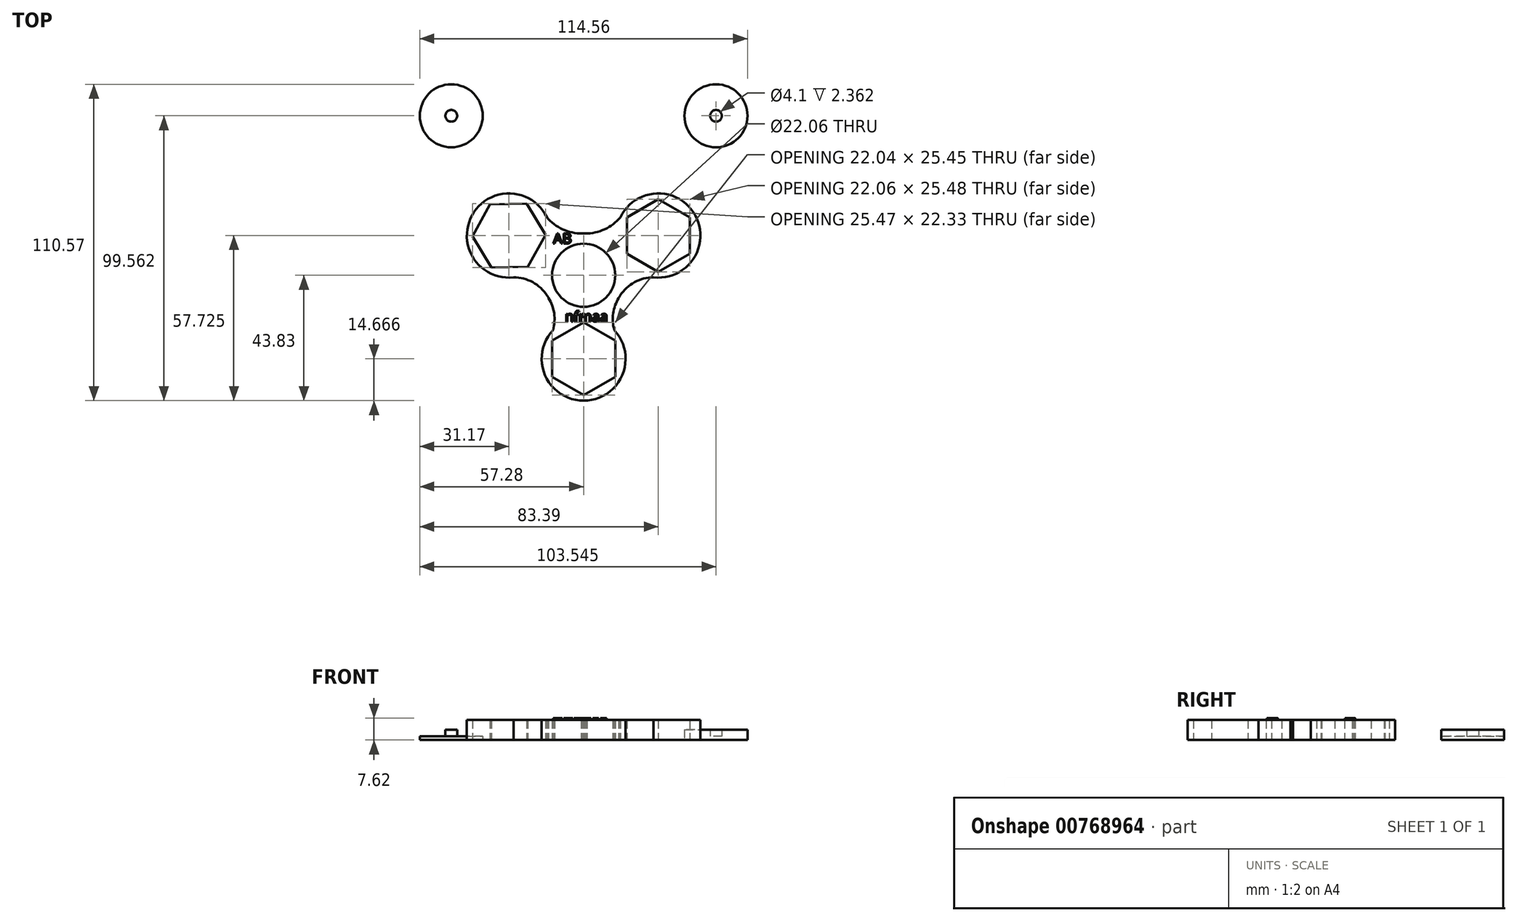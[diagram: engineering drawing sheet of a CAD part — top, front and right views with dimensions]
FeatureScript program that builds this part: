
annotation { "Feature Type Name" : "Feature", "Feature Type Description" : "" }
export const myFeature = defineFeature(function(context is Context, id is Id, definition is map)
    precondition{}
    {
        {
            var Q0;
            Q0=qCreatedBy(makeId("Top.planeOp"),FACE);
            var sketch = newSketch(context, id + "F0", { "sketchPlane" : qUnion([Q0])});
            skCircle(sketch, "E0", {"center": v(0, 0) * mm, "radius": 11.03 * mm});
            skCircle(sketch, "E1", {"center": v(0, 0) * mm, "radius": 14.6 * mm});
            skPoint(sketch, "E2", {"position": v(26.11, 13.9) * mm});
            skCircle(sketch, "E3", {"center": v(26.11, 13.9) * mm, "radius": 14.7 * mm});
            skPoint(sketch, "E4.MirrorP", {"position": v(-26.11, 13.9) * mm});
            skCircle(sketch, "E5.MirrorC", {"center": v(-26.11, 13.9) * mm, "radius": 14.7 * mm});
            skCircle(sketch, "E6", {"center": v(0, -29.16) * mm, "radius": 14.66 * mm});
            skLineSegment(sketch, "E7.0", {"start": v(-13.37, 14.17) * mm, "end": v(-19.5, 3) * mm});
            skLineSegment(sketch, "E7.1", {"start": v(-19.5, 3) * mm, "end": v(-32.24, 2.73) * mm});
            skLineSegment(sketch, "E7.2", {"start": v(-32.24, 2.73) * mm, "end": v(-38.85, 13.62) * mm});
            skLineSegment(sketch, "E7.3", {"start": v(-38.85, 13.62) * mm, "end": v(-32.71, 24.79) * mm});
            skLineSegment(sketch, "E7.4", {"start": v(-32.71, 24.79) * mm, "end": v(-19.98, 25.06) * mm});
            skLineSegment(sketch, "E7.5", {"start": v(-19.98, 25.06) * mm, "end": v(-13.37, 14.17) * mm});
            skLineSegment(sketch, "E8.0", {"start": v(37.14, 20.26) * mm, "end": v(37.14, 7.53) * mm});
            skLineSegment(sketch, "E8.1", {"start": v(37.14, 7.53) * mm, "end": v(26.11, 1.16) * mm});
            skLineSegment(sketch, "E8.2", {"start": v(26.11, 1.16) * mm, "end": v(15.08, 7.53) * mm});
            skLineSegment(sketch, "E8.3", {"start": v(15.08, 7.53) * mm, "end": v(15.08, 20.26) * mm});
            skLineSegment(sketch, "E8.4", {"start": v(15.08, 20.26) * mm, "end": v(26.11, 26.63) * mm});
            skLineSegment(sketch, "E8.5", {"start": v(26.11, 26.63) * mm, "end": v(37.14, 20.26) * mm});
            skLineSegment(sketch, "E9.0", {"start": v(-11.02, -35.53) * mm, "end": v(-11.02, -22.8) * mm});
            skLineSegment(sketch, "E9.1", {"start": v(-11.02, -22.8) * mm, "end": v(0, -16.44) * mm});
            skLineSegment(sketch, "E9.2", {"start": v(0, -16.44) * mm, "end": v(11.02, -22.8) * mm});
            skLineSegment(sketch, "E9.3", {"start": v(11.02, -22.8) * mm, "end": v(11.02, -35.53) * mm});
            skLineSegment(sketch, "E9.4", {"start": v(11.02, -35.53) * mm, "end": v(0, -41.89) * mm});
            skLineSegment(sketch, "E9.5", {"start": v(0, -41.89) * mm, "end": v(-11.02, -35.53) * mm});
            skArc(sketch, "E10", {"start": v(0, 14.6) * mm, "mid": v(7.07, 15.96) * mm, "end": v(12.85, 20.26) * mm});
            skArc(sketch, "E11.MirrorCS", {"start": v(0, 14.6) * mm, "mid": v(-7.07, 15.96) * mm, "end": v(-12.85, 20.26) * mm});
            skArc(sketch, "E12", {"start": v(26.11, -0.81) * mm, "mid": v(18.1, -2.27) * mm, "end": v(12.25, -7.95) * mm});
            skArc(sketch, "E13.MirrorCS", {"start": v(-26.11, -0.81) * mm, "mid": v(-18.1, -2.27) * mm, "end": v(-12.25, -7.95) * mm});
            skArc(sketch, "E14", {"start": v(12.25, -7.95) * mm, "mid": v(10.18, -15.38) * mm, "end": v(12.25, -22.8) * mm});
            skArc(sketch, "E15.MirrorCS", {"start": v(-12.25, -7.95) * mm, "mid": v(-10.18, -15.38) * mm, "end": v(-12.25, -22.8) * mm});
            skSolve(sketch);
        }
        {
            var Q0;
            Q0=qSketchRegion(id+"F0",true);
            extrude(context, id + "F1", {"entities" : qUnion([Q0]), "depth" : 7 * mm, "offsetDistance" : 25.4 * mm});
        }
        {
            var Q0;
            Q0=qCreatedBy(makeId("Top.planeOp"),FACE);
            var sketch = newSketch(context, id + "F2", { "sketchPlane" : qUnion([Q0])});
            skText(sketch, "E16", { "text": "nfmaa", "fontName": "OpenSans-Regular.ttf"});
            skText(sketch, "E17", { "text": "AB", "fontName": "OpenSans-Regular.ttf"});
            const initialGuessF2  = {"E16": [-0.00651, -0.01619, 1, 0, 0.0036], "E17": [-0.0106, 0.01111, 1, 0, 0.0036]};
            skSetInitialGuess(sketch, initialGuessF2);
            skSolve(sketch);
        }
        {
            var Q0;
            Q0=qSketchRegion(id+"F2",true);
            extrude(context, id + "F3", {"entities" : qUnion([Q0]), "operationType" : NewBodyOperationType.ADD, "depth" : 7.62 * mm, "offsetDistance" : 25.4 * mm});
        }
        {
            var Q0;
            Q0=qCreatedBy(makeId("Top.planeOp"),FACE);
            var sketch = newSketch(context, id + "F4", { "sketchPlane" : qUnion([Q0])});
            skCircle(sketch, "E18", {"center": v(-46.27, 55.73) * mm, "radius": 2.05 * mm});
            skCircle(sketch, "E19.MirrorC", {"center": v(46.27, 55.73) * mm, "radius": 2.05 * mm});
            skCircle(sketch, "E20", {"center": v(-46.27, 55.73) * mm, "radius": 11.01 * mm});
            skCircle(sketch, "E21.MirrorC", {"center": v(46.27, 55.73) * mm, "radius": 11.01 * mm});
            skSolve(sketch);
        }
        {
            var Q0;
            Q0=makeQuery(id+"F4.imprint","IMPRINT",FACE,{"disambiguationData":[TD([[makeQuery(id+"F4.imprint","IMPRINT",EDGE,{"derivedFrom":sQuery(id+"F4.wireOp",EDGE,"E18")}),1.0]])]});
            extrude(context, id + "F5", {"entities" : qUnion([Q0]), "depth" : 3.63 * mm, "offsetDistance" : 25.4 * mm});
        }
        {
            var Q0;
            Q0=makeQuery(id+"F4.imprint","IMPRINT",FACE,{"disambiguationData":[TD([[makeQuery(id+"F4.imprint","IMPRINT",EDGE,{"derivedFrom":sQuery(id+"F4.wireOp",EDGE,"E18")}),-1.0]])]});
            extrude(context, id + "F6", {"entities" : qUnion([Q0]), "operationType" : NewBodyOperationType.ADD, "depth" : 1.27 * mm, "offsetDistance" : 25.4 * mm});
        }
        {
            var Q0;
            Q0=makeQuery(id+"F4.imprint","IMPRINT",FACE,{"disambiguationData":[TD([[makeQuery(id+"F4.imprint","IMPRINT",EDGE,{"derivedFrom":sQuery(id+"F4.wireOp",EDGE,"E19.MirrorC")}),-1.0]])]});
            extrude(context, id + "F7", {"entities" : qUnion([Q0]), "depth" : 3.63 * mm, "offsetDistance" : 25.4 * mm});
        }
        {
            var Q0;
            Q0=makeQuery(id+"F4.imprint","IMPRINT",FACE,{"disambiguationData":[TD([[makeQuery(id+"F4.imprint","IMPRINT",EDGE,{"derivedFrom":sQuery(id+"F4.wireOp",EDGE,"E19.MirrorC")}),1.0]])]});
            extrude(context, id + "F8", {"entities" : qUnion([Q0]), "operationType" : NewBodyOperationType.ADD, "depth" : 1.27 * mm, "offsetDistance" : 25.4 * mm});
        }
    });
